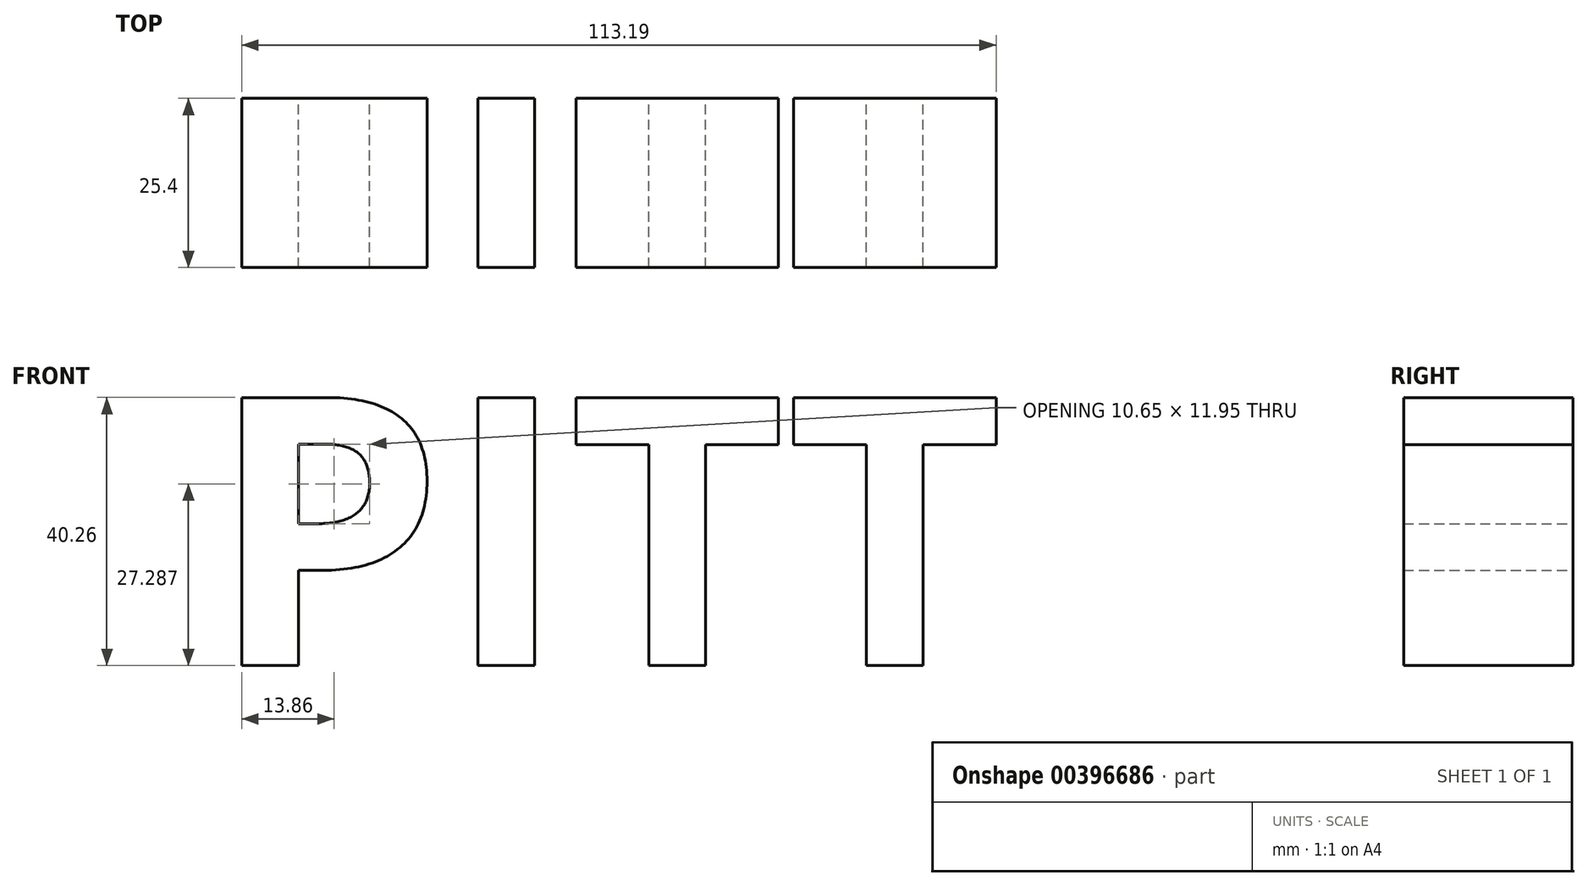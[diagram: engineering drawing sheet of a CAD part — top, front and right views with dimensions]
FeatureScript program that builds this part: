
annotation { "Feature Type Name" : "Feature", "Feature Type Description" : "" }
export const myFeature = defineFeature(function(context is Context, id is Id, definition is map)
    precondition{}
    {
        {
            var Q0;
            Q0=qCreatedBy(makeId("Front.planeOp"),FACE);
            var sketch = newSketch(context, id + "F0", { "sketchPlane" : qUnion([Q0])});
            skCircle(sketch, "E0", {"center": v(0, 0) * mm, "radius": 64.27 * mm});
            skText(sketch, "E1", { "text": "PITT", "fontName": "OpenSans-Bold.ttf"});
            const initialGuessF0  = {"E1": [-0.06115, -0.02085, 1, 0, 0.0406]};
            skSetInitialGuess(sketch, initialGuessF0);
            skSolve(sketch);
        }
        {
            var Q0;
            Q0=makeQuery(id+"F0.imprint","IMPRINT",FACE,{"disambiguationData":[TD([[makeQuery(id+"F0.imprint","IMPRINT",EDGE,{"derivedFrom":sQuery(id+"F0.wireOp",EDGE,"E1.sketch_text.stroke-0")}),-1.0]])]});
            var Q1;
            Q1=makeQuery(id+"F0.imprint","IMPRINT",FACE,{"disambiguationData":[TD([[makeQuery(id+"F0.imprint","IMPRINT",EDGE,{"derivedFrom":sQuery(id+"F0.wireOp",EDGE,"E1.sketch_text.stroke-16")}),-1.0]])]});
            var Q2;
            Q2=makeQuery(id+"F0.imprint","IMPRINT",FACE,{"disambiguationData":[TD([[makeQuery(id+"F0.imprint","IMPRINT",EDGE,{"derivedFrom":sQuery(id+"F0.wireOp",EDGE,"E1.sketch_text.stroke-20")}),-1.0]])]});
            var Q3;
            Q3=makeQuery(id+"F0.imprint","IMPRINT",FACE,{"disambiguationData":[TD([[makeQuery(id+"F0.imprint","IMPRINT",EDGE,{"derivedFrom":sQuery(id+"F0.wireOp",EDGE,"E1.sketch_text.stroke-28")}),-1.0]])]});
            extrude(context, id + "F1", {"entities" : qUnion([Q0, Q1, Q2, Q3]), "depth" : 25.4 * mm});
        }
    });
